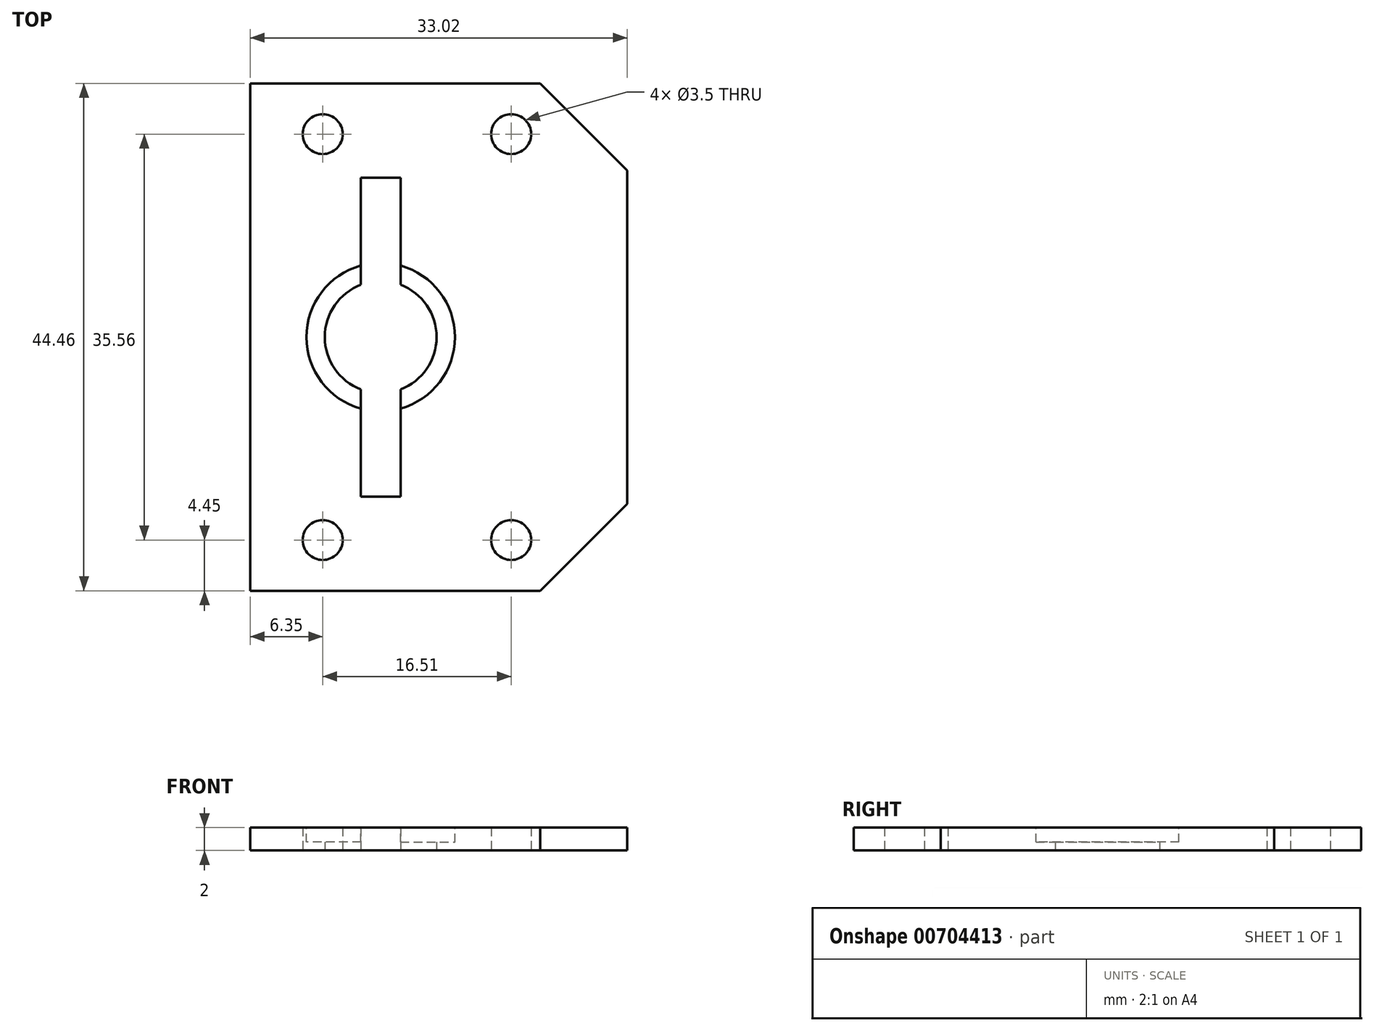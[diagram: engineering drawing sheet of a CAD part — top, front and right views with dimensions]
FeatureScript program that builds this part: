
annotation { "Feature Type Name" : "Feature", "Feature Type Description" : "" }
export const myFeature = defineFeature(function(context is Context, id is Id, definition is map)
    precondition{}
    {
        {
            var Q0;
            Q0=qCreatedBy(makeId("Top.planeOp"),FACE);
            var sketch = newSketch(context, id + "F0", { "sketchPlane" : qUnion([Q0])});
            skLineSegment(sketch, "E0.bottom", {"start": v(0, -22.23) * mm, "end": v(33.02, -22.23) * mm});
            skLineSegment(sketch, "E0.top", {"start": v(0, 22.23) * mm, "end": v(33.02, 22.22) * mm});
            skLineSegment(sketch, "E0.left", {"start": v(0, -22.23) * mm, "end": v(0, 22.23) * mm});
            skLineSegment(sketch, "E0.right", {"start": v(33.02, -22.23) * mm, "end": v(33.02, 22.23) * mm});
            skLineSegment(sketch, "E1", {"start": v(0, 0) * mm, "end": v(33.02, 0) * mm, "construction": true});
            skCircle(sketch, "E2", {"center": v(6.35, 17.78) * mm, "radius": 1.75 * mm});
            skCircle(sketch, "E3", {"center": v(22.86, 17.78) * mm, "radius": 1.75 * mm});
            skCircle(sketch, "E4.MirrorC", {"center": v(6.35, -17.78) * mm, "radius": 1.75 * mm});
            skCircle(sketch, "E5.MirrorC", {"center": v(22.86, -17.78) * mm, "radius": 1.75 * mm});
            skCircle(sketch, "E6", {"center": v(11.43, 0) * mm, "radius": 4.9 * mm});
            skLineSegment(sketch, "E7", {"start": v(11.43, 0) * mm, "end": v(11.43, 13.97) * mm, "construction": true});
            skLineSegment(sketch, "E8", {"start": v(11.43, 13.97) * mm, "end": v(9.7, 13.97) * mm});
            skLineSegment(sketch, "E9", {"start": v(9.7, 13.97) * mm, "end": v(9.7, 0) * mm});
            skLineSegment(sketch, "E10.MirrorCS", {"start": v(13.17, 13.97) * mm, "end": v(13.17, 0) * mm});
            skLineSegment(sketch, "E11.MirrorCS", {"start": v(11.43, 13.97) * mm, "end": v(13.17, 13.97) * mm});
            skLineSegment(sketch, "E12.MirrorCS", {"start": v(9.7, -13.97) * mm, "end": v(9.7, 0) * mm});
            skLineSegment(sketch, "E13.MirrorCS", {"start": v(11.43, -13.97) * mm, "end": v(9.7, -13.97) * mm});
            skLineSegment(sketch, "E14.MirrorCS", {"start": v(11.43, -13.97) * mm, "end": v(13.17, -13.97) * mm});
            skLineSegment(sketch, "E15.MirrorCS", {"start": v(13.17, -13.97) * mm, "end": v(13.17, 0) * mm});
            skSolve(sketch);
        }
        {
            var Q0;
            Q0 = qSketchRegion(id + "F0", true);
            extrude(context, id + "F1", {"entities" : qUnion([Q0]), "depth" : 2 * mm, "offsetDistance" : 25.4 * mm});
        }
        {
            var Q0;
            Q0=makeQuery(id+"F1.opExtrude","SWEPT_EDGE",EDGE,{"disambiguationData":[OSD([sQuery(id+"F0.wireOp",EDGE,"E0.bottom"),sQuery(id+"F0.wireOp",EDGE,"E0.right")])]});
            var Q1;
            Q1=makeQuery(id+"F1.opExtrude","SWEPT_EDGE",EDGE,{"disambiguationData":[OSD([sQuery(id+"F0.wireOp",EDGE,"E0.top"),sQuery(id+"F0.wireOp",EDGE,"E0.right")])]});
            chamfer(context, id + "F2", {"entities" : qUnion([Q0, Q1]), "width" : 7.62 * mm, "tangentPropagation" : true});
        }
        {
            var Q0;
            Q0=makeQuery(id+"F1.opExtrude","CAP_FACE",FACE,{"disambiguationData":[OSD([sQuery(id+"F0.wireOp",EDGE,"E0.bottom"),sQuery(id+"F0.wireOp",EDGE,"E0.top"),sQuery(id+"F0.wireOp",EDGE,"E0.left"),sQuery(id+"F0.wireOp",EDGE,"E0.right"),sQuery(id+"F0.wireOp",EDGE,"E2"),sQuery(id+"F0.wireOp",EDGE,"E3"),sQuery(id+"F0.wireOp",EDGE,"E4.MirrorC"),sQuery(id+"F0.wireOp",EDGE,"E5.MirrorC"),sQuery(id+"F0.wireOp",EDGE,"E6"),sQuery(id+"F0.wireOp",EDGE,"E8"),sQuery(id+"F0.wireOp",EDGE,"E9"),sQuery(id+"F0.wireOp",EDGE,"E10.MirrorCS"),sQuery(id+"F0.wireOp",EDGE,"E11.MirrorCS"),sQuery(id+"F0.wireOp",EDGE,"E12.MirrorCS"),sQuery(id+"F0.wireOp",EDGE,"E13.MirrorCS"),sQuery(id+"F0.wireOp",EDGE,"E14.MirrorCS"),sQuery(id+"F0.wireOp",EDGE,"E15.MirrorCS")])],"isStart":false});
            var sketch = newSketch(context, id + "F3", { "sketchPlane" : qUnion([Q0])});
            skCircle(sketch, "E16", {"center": v(11.43, 0) * mm, "radius": 6.5 * mm});
            skSolve(sketch);
        }
        {
            var Q0;
            Q0 = qSketchRegion(id + "F3", true);
            extrude(context, id + "F4", {"entities" : qUnion([Q0]), "operationType" : NewBodyOperationType.REMOVE, "oppositeDirection" : true, "depth" : 1.27 * mm, "offsetDistance" : 25.4 * mm});
        }
    });
